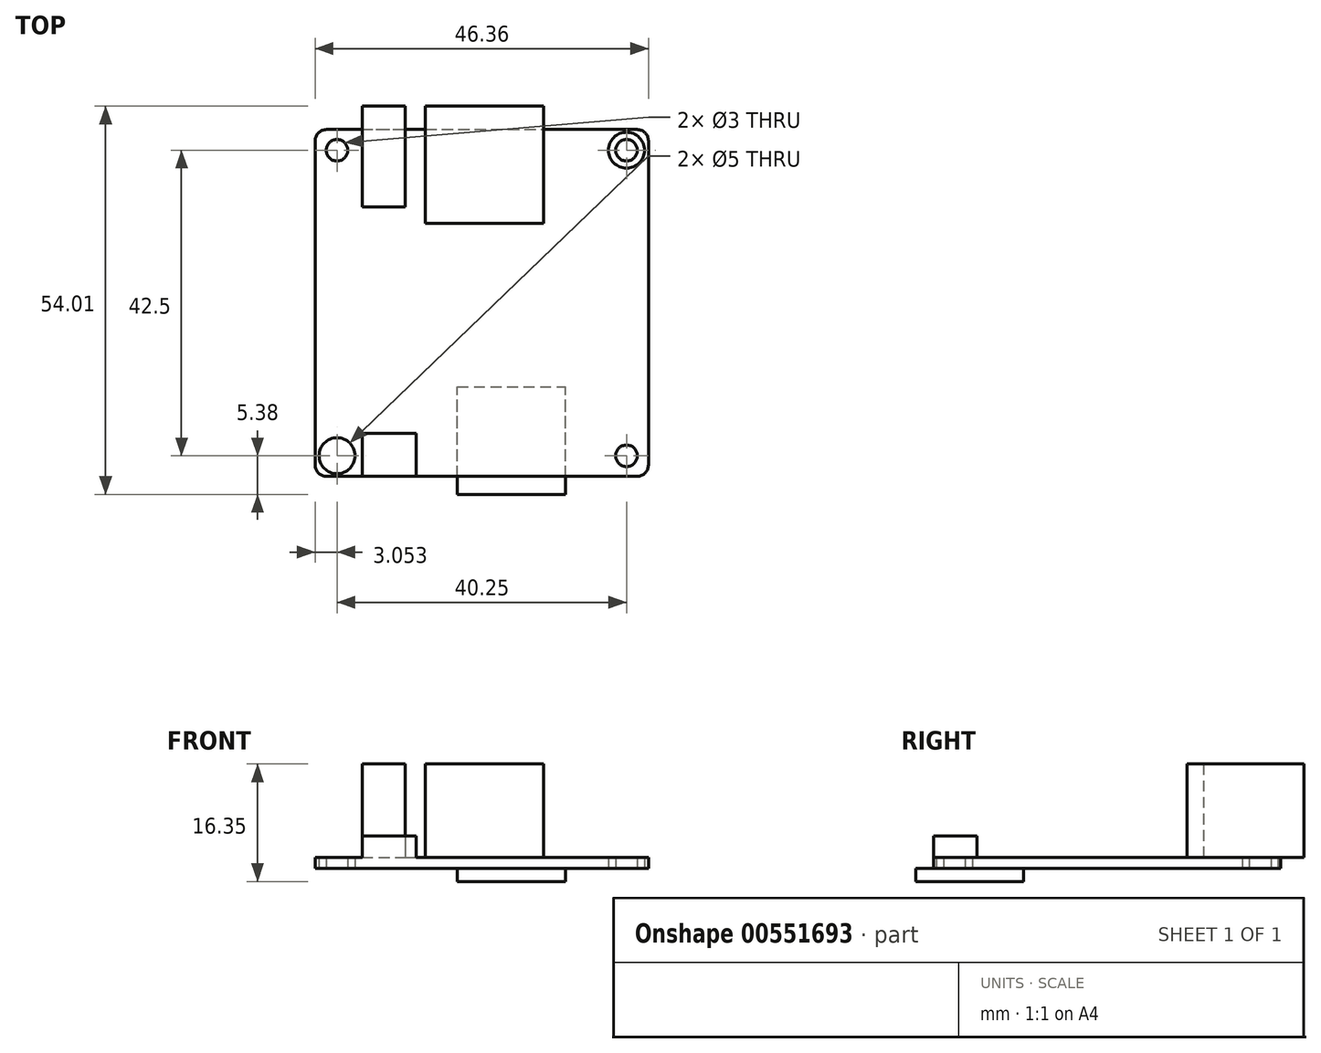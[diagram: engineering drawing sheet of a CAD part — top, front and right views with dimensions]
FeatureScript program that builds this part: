
annotation { "Feature Type Name" : "Feature", "Feature Type Description" : "" }
export const myFeature = defineFeature(function(context is Context, id is Id, definition is map)
    precondition{}
    {
        {
            var Q0;
            Q0=qCreatedBy(makeId("Top.planeOp"),FACE);
            var sketch = newSketch(context, id + "F0", { "sketchPlane" : qUnion([Q0])});
            skLineSegment(sketch, "E0.bottom", {"start": v(1.59, 0) * mm, "end": v(44.77, 0) * mm});
            skLineSegment(sketch, "E0.top", {"start": v(1.59, 48.26) * mm, "end": v(44.77, 48.26) * mm});
            skLineSegment(sketch, "E0.left", {"start": v(0, 1.59) * mm, "end": v(0, 46.67) * mm});
            skLineSegment(sketch, "E0.right", {"start": v(46.35, 1.59) * mm, "end": v(46.35, 46.67) * mm});
            skCircle(sketch, "E1", {"center": v(43.3, 2.88) * mm, "radius": 2.5 * mm});
            skLineSegment(sketch, "E2", {"start": v(23.18, 48.26) * mm, "end": v(23.18, 0) * mm, "construction": true});
            skLineSegment(sketch, "E3", {"start": v(0, 24.13) * mm, "end": v(46.35, 24.13) * mm, "construction": true});
            skCircle(sketch, "E4", {"center": v(43.3, 2.88) * mm, "radius": 1.5 * mm});
            skCircle(sketch, "E5.MirrorC", {"center": v(43.3, 45.38) * mm, "radius": 1.5 * mm});
            skCircle(sketch, "E6.MirrorC", {"center": v(43.3, 45.38) * mm, "radius": 2.5 * mm});
            skCircle(sketch, "E7.MirrorC", {"center": v(3.05, 2.88) * mm, "radius": 2.5 * mm});
            skCircle(sketch, "E8.MirrorC", {"center": v(3.05, 45.38) * mm, "radius": 2.5 * mm});
            skCircle(sketch, "E9.MirrorC", {"center": v(3.05, 45.38) * mm, "radius": 1.5 * mm});
            skCircle(sketch, "E10.MirrorC", {"center": v(3.05, 2.88) * mm, "radius": 1.5 * mm});
            skPoint(sketch, "E11.visualSharp", {"position": v(0, 48.26) * mm});
            skArc(sketch, "E11.filletArc", {"start": v(1.59, 48.26) * mm, "mid": v(0.46, 47.8) * mm, "end": v(0, 46.67) * mm});
            skPoint(sketch, "E12.visualSharp", {"position": v(46.35, 48.26) * mm});
            skArc(sketch, "E12.filletArc", {"start": v(46.35, 46.67) * mm, "mid": v(45.9, 47.8) * mm, "end": v(44.77, 48.26) * mm});
            skPoint(sketch, "E13.visualSharp", {"position": v(0, 0) * mm});
            skArc(sketch, "E13.filletArc", {"start": v(0, 1.59) * mm, "mid": v(0.46, 0.46) * mm, "end": v(1.59, 0) * mm});
            skPoint(sketch, "E14.visualSharp", {"position": v(46.35, 0) * mm});
            skArc(sketch, "E14.filletArc", {"start": v(44.77, 0) * mm, "mid": v(45.9, 0.46) * mm, "end": v(46.35, 1.59) * mm});
            skSolve(sketch);
        }
        {
            var Q0;
            Q0=makeQuery(id+"F0.imprint","IMPRINT",FACE,{"disambiguationData":[TD([[makeQuery(id+"F0.imprint","IMPRINT",EDGE,{"derivedFrom":sQuery(id+"F0.wireOp",EDGE,"E0.bottom")}),1.0]])]});
            var Q1;
            Q1=makeQuery(id+"F0.imprint","IMPRINT",FACE,{"disambiguationData":[TD([[makeQuery(id+"F0.imprint","IMPRINT",EDGE,{"derivedFrom":sQuery(id+"F0.wireOp",EDGE,"E7.MirrorC")}),-1.0]])]});
            var Q2;
            Q2=makeQuery(id+"F0.imprint","IMPRINT",FACE,{"disambiguationData":[TD([[makeQuery(id+"F0.imprint","IMPRINT",EDGE,{"derivedFrom":sQuery(id+"F0.wireOp",EDGE,"E1")}),1.0]])]});
            var Q3;
            Q3=makeQuery(id+"F0.imprint","IMPRINT",FACE,{"disambiguationData":[TD([[makeQuery(id+"F0.imprint","IMPRINT",EDGE,{"derivedFrom":sQuery(id+"F0.wireOp",EDGE,"E5.MirrorC")}),1.0]])]});
            var Q4;
            Q4=makeQuery(id+"F0.imprint","IMPRINT",FACE,{"disambiguationData":[TD([[makeQuery(id+"F0.imprint","IMPRINT",EDGE,{"derivedFrom":sQuery(id+"F0.wireOp",EDGE,"E8.MirrorC")}),1.0]])]});
            extrude(context, id + "F1", {"entities" : qUnion([Q0, Q1, Q2, Q3, Q4]), "depth" : 1.5 * mm});
        }
        {
            var Q0;
            Q0=makeQuery(id+"F1.opExtrude","CAP_FACE",FACE,{"disambiguationData":[OSD([sQuery(id+"F0.wireOp",EDGE,"E0.bottom"),sQuery(id+"F0.wireOp",EDGE,"E0.top"),sQuery(id+"F0.wireOp",EDGE,"E0.left"),sQuery(id+"F0.wireOp",EDGE,"E0.right"),sQuery(id+"F0.wireOp",EDGE,"E4"),sQuery(id+"F0.wireOp",EDGE,"E5.MirrorC"),sQuery(id+"F0.wireOp",EDGE,"E9.MirrorC"),sQuery(id+"F0.wireOp",EDGE,"E10.MirrorC"),sQuery(id+"F0.wireOp",EDGE,"E11.filletArc"),sQuery(id+"F0.wireOp",EDGE,"E12.filletArc"),sQuery(id+"F0.wireOp",EDGE,"E13.filletArc"),sQuery(id+"F0.wireOp",EDGE,"E14.filletArc")])],"isStart":false});
            var sketch = newSketch(context, id + "F2", { "sketchPlane" : qUnion([Q0])});
            skLineSegment(sketch, "E15.bottom", {"start": v(6.55, 51.51) * mm, "end": v(12.55, 51.51) * mm});
            skLineSegment(sketch, "E15.top", {"start": v(6.55, 37.51) * mm, "end": v(12.55, 37.51) * mm});
            skLineSegment(sketch, "E15.left", {"start": v(6.55, 51.51) * mm, "end": v(6.55, 37.51) * mm});
            skLineSegment(sketch, "E15.right", {"start": v(12.55, 51.51) * mm, "end": v(12.55, 37.51) * mm});
            skLineSegment(sketch, "E16.bottom", {"start": v(15.3, 51.51) * mm, "end": v(31.8, 51.51) * mm});
            skLineSegment(sketch, "E16.top", {"start": v(15.3, 35.21) * mm, "end": v(31.8, 35.21) * mm});
            skLineSegment(sketch, "E16.left", {"start": v(15.3, 51.51) * mm, "end": v(15.3, 35.21) * mm});
            skLineSegment(sketch, "E16.right", {"start": v(31.8, 51.51) * mm, "end": v(31.8, 35.21) * mm});
            skLineSegment(sketch, "E17.bottom", {"start": v(6.55, 0) * mm, "end": v(14.05, 0) * mm});
            skLineSegment(sketch, "E17.top", {"start": v(6.55, 6) * mm, "end": v(14.05, 6) * mm});
            skLineSegment(sketch, "E17.left", {"start": v(6.55, 0) * mm, "end": v(6.55, 6) * mm});
            skLineSegment(sketch, "E17.right", {"start": v(14.05, 0) * mm, "end": v(14.05, 6) * mm});
            skLineSegment(sketch, "E18.bottom", {"start": v(19.8, -2.5) * mm, "end": v(34.8, -2.5) * mm});
            skLineSegment(sketch, "E18.top", {"start": v(19.8, 12.5) * mm, "end": v(34.8, 12.5) * mm});
            skLineSegment(sketch, "E18.left", {"start": v(19.8, -2.5) * mm, "end": v(19.8, 12.5) * mm});
            skLineSegment(sketch, "E18.right", {"start": v(34.8, -2.5) * mm, "end": v(34.8, 12.5) * mm});
            skSolve(sketch);
        }
        {
            var Q0;
            Q0=makeQuery(id+"F2.imprint","IMPRINT",FACE,{"disambiguationData":[TD([[makeQuery(id+"F2.imprint","IMPRINT",EDGE,{"derivedFrom":sQuery(id+"F2.wireOp",EDGE,"E15.bottom")}),-1.0]])]});
            var Q1;
            Q1=makeQuery(id+"F2.imprint","IMPRINT",FACE,{"disambiguationData":[TD([[makeQuery(id+"F2.imprint","IMPRINT",EDGE,{"derivedFrom":sQuery(id+"F2.wireOp",EDGE,"E16.bottom")}),-1.0]])]});
            var Q2;
            {var subQ0=sQuery(id+"F2.wireOp",EDGE,"E15.top");Q2=makeQuery(id+"F2.imprint","IMPRINT",FACE,{"disambiguationData":[TD([[makeQuery(id+"F2.imprint","IMPRINT",EDGE,{"derivedFrom":subQ0}),1.0]])]});}
            var Q3;
            {var subQ0=sQuery(id+"F2.wireOp",EDGE,"E16.top");Q3=makeQuery(id+"F2.imprint","IMPRINT",FACE,{"disambiguationData":[TD([[makeQuery(id+"F2.imprint","IMPRINT",EDGE,{"derivedFrom":subQ0}),1.0]])]});}
            extrude(context, id + "F3", {"entities" : qUnion([Q0, Q1, Q2, Q3]), "operationType" : NewBodyOperationType.ADD, "depth" : 13 * mm});
        }
        {
            var Q0;
            Q0=makeQuery(id+"F2.imprint","IMPRINT",FACE,{"disambiguationData":[TD([[makeQuery(id+"F2.imprint","IMPRINT",EDGE,{"derivedFrom":sQuery(id+"F2.wireOp",EDGE,"E17.bottom")}),1.0]])]});
            extrude(context, id + "F4", {"entities" : qUnion([Q0]), "operationType" : NewBodyOperationType.ADD, "depth" : 3 * mm});
        }
        {
            var Q0;
            Q0=makeQuery(id+"F1.opExtrude","CAP_FACE",FACE,{"disambiguationData":[OSD([sQuery(id+"F0.wireOp",EDGE,"E0.bottom"),sQuery(id+"F0.wireOp",EDGE,"E0.top"),sQuery(id+"F0.wireOp",EDGE,"E0.left"),sQuery(id+"F0.wireOp",EDGE,"E0.right"),sQuery(id+"F0.wireOp",EDGE,"E4"),sQuery(id+"F0.wireOp",EDGE,"E5.MirrorC"),sQuery(id+"F0.wireOp",EDGE,"E9.MirrorC"),sQuery(id+"F0.wireOp",EDGE,"E10.MirrorC"),sQuery(id+"F0.wireOp",EDGE,"E11.filletArc"),sQuery(id+"F0.wireOp",EDGE,"E12.filletArc"),sQuery(id+"F0.wireOp",EDGE,"E13.filletArc"),sQuery(id+"F0.wireOp",EDGE,"E14.filletArc")])],"isStart":true});
            var sketch = newSketch(context, id + "F5", { "sketchPlane" : qUnion([Q0])});
            skLineSegment(sketch, "E19.0", {"start": v(19.8, -12.5) * mm, "end": v(34.8, -12.5) * mm});
            skLineSegment(sketch, "E19.1", {"start": v(19.8, 2.5) * mm, "end": v(19.8, -12.5) * mm});
            skLineSegment(sketch, "E19.2", {"start": v(19.8, 2.5) * mm, "end": v(34.8, 2.5) * mm});
            skLineSegment(sketch, "E19.3", {"start": v(34.8, 2.5) * mm, "end": v(34.8, -12.5) * mm});
            skSolve(sketch);
        }
        {
            var Q0;
            Q0=qSketchRegion(id+"F5",true);
            extrude(context, id + "F6", {"entities" : qUnion([Q0]), "operationType" : NewBodyOperationType.ADD, "depth" : 1.85 * mm});
        }
    });
